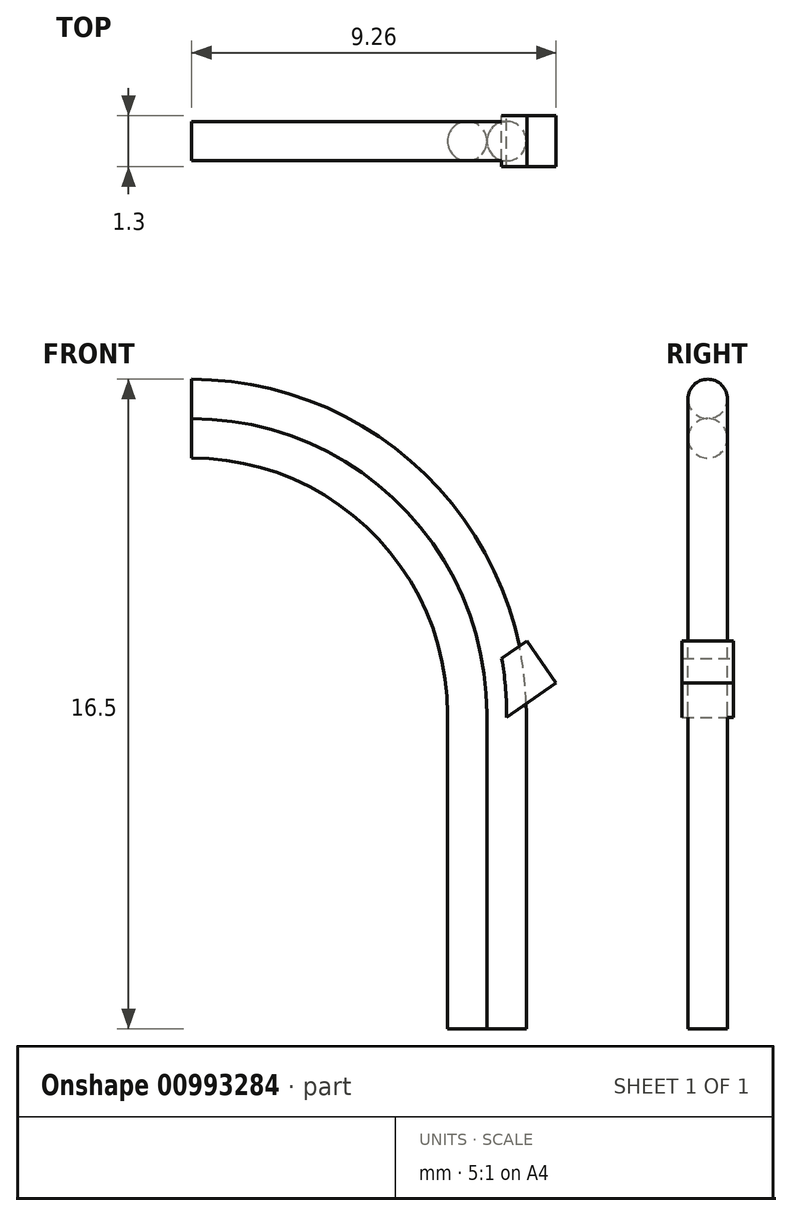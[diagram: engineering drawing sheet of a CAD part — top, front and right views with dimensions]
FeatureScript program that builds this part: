
annotation { "Feature Type Name" : "Feature", "Feature Type Description" : "" }
export const myFeature = defineFeature(function(context is Context, id is Id, definition is map)
    precondition{}
    {
        {
            var Q0;
            Q0=qCreatedBy(makeId("Front.planeOp"),FACE);
            var sketch = newSketch(context, id + "F0", { "sketchPlane" : qUnion([Q0])});
            skCircle(sketch, "E0", {"center": v(-25, 0) * mm, "radius": 11 * mm});
            skCircle(sketch, "E1", {"center": v(22, 0) * mm, "radius": 11.5 * mm});
            skLineSegment(sketch, "E2", {"start": v(-25, 0) * mm, "end": v(-16.63, 23) * mm});
            skLineSegment(sketch, "E3", {"start": v(-19.54, 15) * mm, "end": v(-7, 15) * mm});
            skCircle(sketch, "E4", {"center": v(3, 2) * mm, "radius": 1.5 * mm});
            skLineSegment(sketch, "E5", {"start": v(0, 8) * mm, "end": v(0, 0) * mm});
            skPoint(sketch, "E6.visualSharp", {"position": v(0, 15) * mm});
            skArc(sketch, "E6.filletArc", {"start": v(0, 8) * mm, "mid": v(-2.05, 12.95) * mm, "end": v(-7, 15) * mm});
            skLineSegment(sketch, "E7.0", {"start": v(-19.54, 14) * mm, "end": v(-7, 14) * mm});
            skArc(sketch, "E8.0", {"start": v(-1, 8) * mm, "mid": v(-2.76, 12.24) * mm, "end": v(-7, 14) * mm});
            skLineSegment(sketch, "E9.0", {"start": v(-1, 8) * mm, "end": v(-1, 0) * mm});
            skLineSegment(sketch, "E10.0", {"start": v(-19.54, 16) * mm, "end": v(-7, 16) * mm});
            skArc(sketch, "E11.0", {"start": v(1, 8) * mm, "mid": v(-1.34, 13.66) * mm, "end": v(-7, 16) * mm});
            skLineSegment(sketch, "E12.0", {"start": v(1, 8) * mm, "end": v(1, 0) * mm});
            skLineSegment(sketch, "E13", {"start": v(0, 8) * mm, "end": v(9.77, 14.84) * mm});
            skLineSegment(sketch, "E14", {"start": v(0, 8) * mm, "end": v(10.37, 8) * mm, "construction": true});
            skLineSegment(sketch, "E15.0", {"start": v(1, 8.09) * mm, "end": v(10.06, 14.43) * mm});
            skLineSegment(sketch, "E16.0", {"start": v(0.9, 9.24) * mm, "end": v(9.49, 15.25) * mm});
            skLineSegment(sketch, "E17", {"start": v(1.6, 9.73) * mm, "end": v(2.17, 8.91) * mm});
            skLineSegment(sketch, "E18", {"start": v(2.17, 8.91) * mm, "end": v(2.26, 8.79) * mm});
            skLineSegment(sketch, "E19", {"start": v(1.6, 9.73) * mm, "end": v(1.51, 9.85) * mm});
            skLineSegment(sketch, "E20", {"start": v(1.51, 9.85) * mm, "end": v(0.88, 9.4) * mm});
            skLineSegment(sketch, "E21", {"start": v(2.26, 8.79) * mm, "end": v(1, 7.9) * mm});
            skSolve(sketch);
        }
        {
            var Q0;
            Q0=qCreatedBy(makeId("Top.planeOp"),FACE);
            var sketch = newSketch(context, id + "F1", { "sketchPlane" : qUnion([Q0])});
            skCircle(sketch, "E22", {"center": v(0, 0) * mm, "radius": 0.5 * mm});
            skCircle(sketch, "E23", {"center": v(1, 0) * mm, "radius": 0.5 * mm});
            skSolve(sketch);
        }
        {
            var Q0;
            Q0=makeQuery(id+"F1.imprint","IMPRINT",FACE,{"disambiguationData":[TD([[makeQuery(id+"F1.imprint","IMPRINT",EDGE,{"derivedFrom":sQuery(id+"F1.wireOp",EDGE,"E23")}),1.0]])]});
            var Q1;
            Q1=makeQuery(id+"F1.imprint","IMPRINT",FACE,{"disambiguationData":[TD([[makeQuery(id+"F1.imprint","IMPRINT",EDGE,{"derivedFrom":sQuery(id+"F1.wireOp",EDGE,"E22")}),1.0]])]});
            var Q2;
            Q2=sQuery(id+"F0.wireOp",EDGE,"E5");
            var Q3;
            Q3=sQuery(id+"F0.wireOp",EDGE,"E6.filletArc");
            sweep(context, id + "F2", {"profiles" : qUnion([Q0, Q1]), "path" : qUnion([Q2, Q3])});
        }
        {
            var Q0;
            {var subQ4=sQuery(id+"F0.wireOp",EDGE,"E19");Q0=makeQuery(id+"F0.imprint","IMPRINT",FACE,{"disambiguationData":[TD([[makeQuery(id+"F0.imprint","IMPRINT",EDGE,{"derivedFrom":subQ4}),1.0]])]});}
            var Q1;
            {var subQ0=sQuery(id+"F0.wireOp",EDGE,"E16.0");var subQ1=sQuery(id+"F0.wireOp",EDGE,"E11.0");var subQ2=makeQuery(id+"F0.imprint","INTERSECT",VERTEX,{"derivedFrom":[subQ1,subQ0]});Q1=makeQuery(id+"F0.imprint","IMPRINT",FACE,{"disambiguationData":[TD([[makeQuery(id+"F0.imprint","IMPRINT",EDGE,{"disambiguationData":[TD([[subQ2,1.0]])],"derivedFrom":subQ1}),-1.0]])]});}
            var Q2;
            {var subQ0=sQuery(id+"F0.wireOp",EDGE,"E18");Q2=makeQuery(id+"F0.imprint","IMPRINT",FACE,{"disambiguationData":[TD([[makeQuery(id+"F0.imprint","IMPRINT",EDGE,{"derivedFrom":subQ0}),-1.0]])]});}
            var Q3;
            {var subQ0=sQuery(id+"F0.wireOp",EDGE,"E15.0");var subQ1=sQuery(id+"F0.wireOp",EDGE,"E11.0");var subQ2=makeQuery(id+"F0.imprint","INTERSECT",VERTEX,{"derivedFrom":[subQ1,subQ0]});Q3=makeQuery(id+"F0.imprint","IMPRINT",FACE,{"disambiguationData":[TD([[makeQuery(id+"F0.imprint","IMPRINT",EDGE,{"disambiguationData":[TD([[subQ2,-1.0]])],"derivedFrom":subQ1}),-1.0]])]});}
            extrude(context, id + "F3", {"entities" : qUnion([Q0, Q1, Q2, Q3]), "endBound" : BoundingType.SYMMETRIC, "depth" : 1.3 * mm, "offsetDistance" : 25 * mm});
        }
    });
